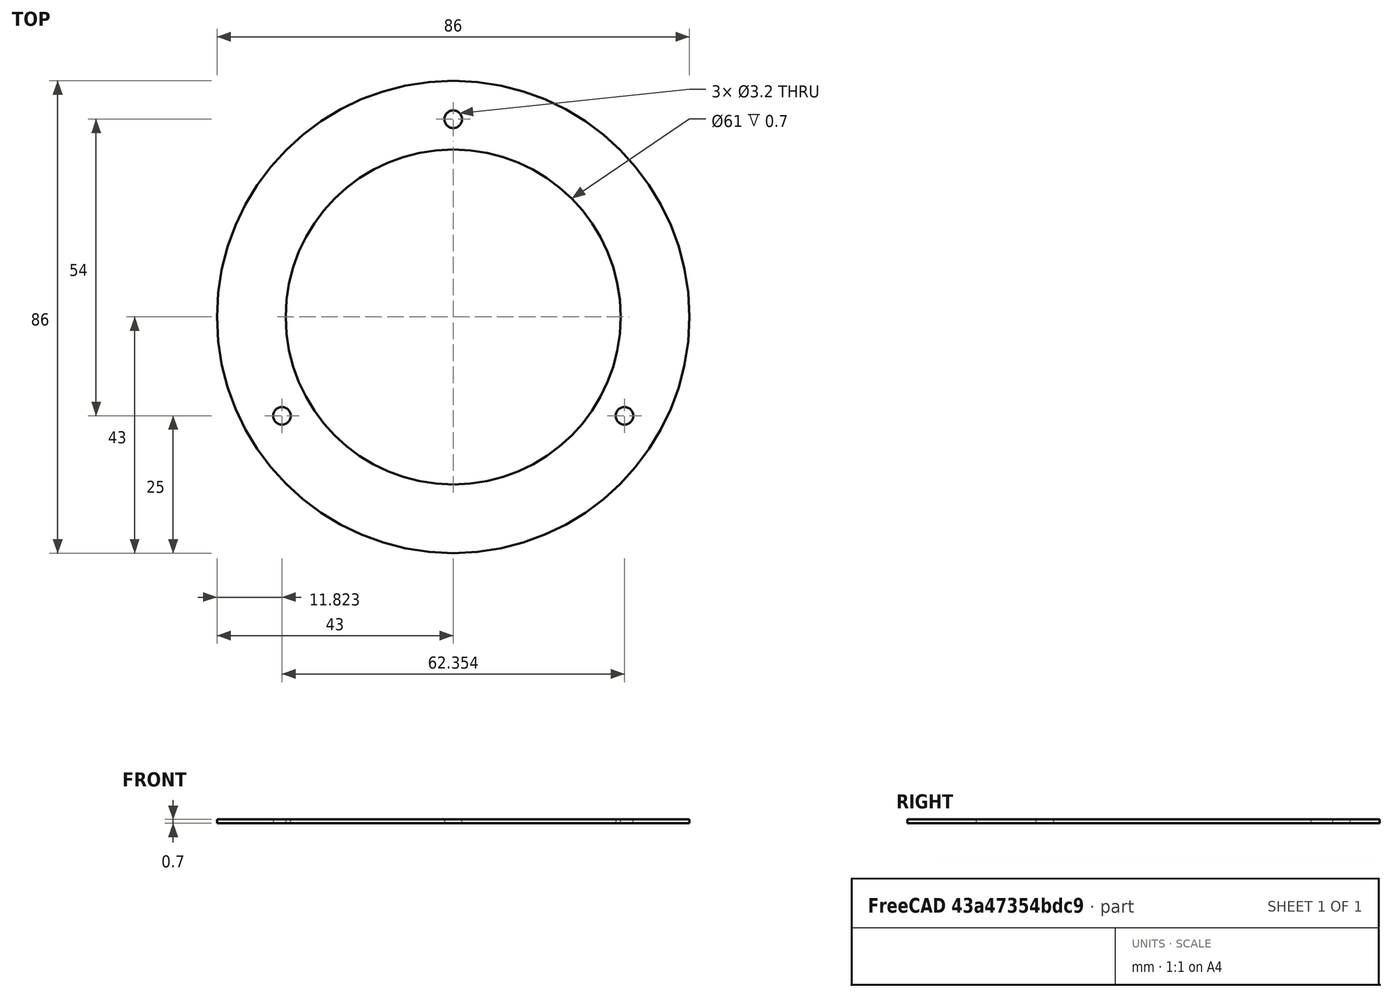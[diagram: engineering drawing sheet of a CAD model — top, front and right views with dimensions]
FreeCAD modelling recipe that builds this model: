
FCSTD DOCUMENT  (FreeCAD 0.19R24276 (Git))
Label: Ring_underglass_h_0_7mm_V4
License: All rights reserved
LicenseURL: http://en.wikipedia.org/wiki/All_rights_reserved
objects: Sketcher::SketchObject×1, PartDesign::Pad×1, PartDesign::Body×1
note: 4 computed .brp shape members not serialized (recipe doc carries the construction recipe); baked Part::Feature solids carry a one-line shape summary decoded from their .brp

FEATURE [Sketcher::SketchObject] Sketch006  label="Sketch006_d72_3_otv_d3.2"
  FullyConstrained = true
  MapMode = 5
  Placement = pos=(0,0,22) rot=(0,0,1;0rad)
  sketch-geometry (9):
    g0: LineSegment StartX=0 StartY=36 StartZ=0 EndX=-31.1769 EndY=-18 EndZ=0
    g1: LineSegment StartX=-31.1769 StartY=-18 StartZ=0 EndX=31.1769 EndY=-18 EndZ=0
    g2: LineSegment StartX=31.1769 StartY=-18 StartZ=0 EndX=0 EndY=36 EndZ=0
    g3: Circle CenterX=0 CenterY=0 CenterZ=0 NormalX=0 NormalY=0 NormalZ=1 AngleXU=0 Radius=36
    g4: Circle CenterX=0 CenterY=36 CenterZ=0 NormalX=0 NormalY=0 NormalZ=1 AngleXU=0 Radius=1.6
    g5: Circle CenterX=31.1769 CenterY=-18 CenterZ=0 NormalX=0 NormalY=0 NormalZ=1 AngleXU=0 Radius=1.6
    g6: Circle CenterX=-31.1769 CenterY=-18 CenterZ=0 NormalX=0 NormalY=0 NormalZ=1 AngleXU=0 Radius=1.6
    g7: Circle CenterX=0 CenterY=0 CenterZ=0 NormalX=0 NormalY=0 NormalZ=1 AngleXU=0 Radius=43
    g8: Circle CenterX=0 CenterY=0 CenterZ=0 NormalX=0 NormalY=0 NormalZ=1 AngleXU=0 Radius=30.5
  constraints (21):
    c: Coincident(g0,g1)
    c: Coincident(g1,g2)
    c: Coincident(g2,g0)
    c: Equal(g0,g1)
    c: Equal(g0,g2)
    c: PointOnObject(g0,g3)
    c: PointOnObject(g1,g3)
    c: PointOnObject(g2,g3)
    c: Coincident(g3,g-1)
    c: PointOnObject(g2,g-2)
    c: Diameter(g3) = 72
    c: Coincident(g4,g0)
    c: Coincident(g5,g1)
    c: Coincident(g6,g0)
    c: Diameter(g6) = 3.2
    c: Equal(g6,g4)
    c: Equal(g6,g5)
    c: Coincident(g7,g-1)
    c: Diameter(g7) = 86
    c: Coincident(g8,g7)
    c: Diameter(g8) = 61
FEATURE [PartDesign::Pad] Pad  label="Pad_h0,7"
  Direction = (1,1,1)
  Length = 0.7
  Length2 = 100
  Placement = pos=(0,0,22) rot=(0,0,1;0rad)
  Profile = -> Sketch006
  Type = 0
FEATURE [PartDesign::Body] Body
  Group = -> [Sketch006,Pad]
  Origin = -> Origin
  Tip = -> Pad
